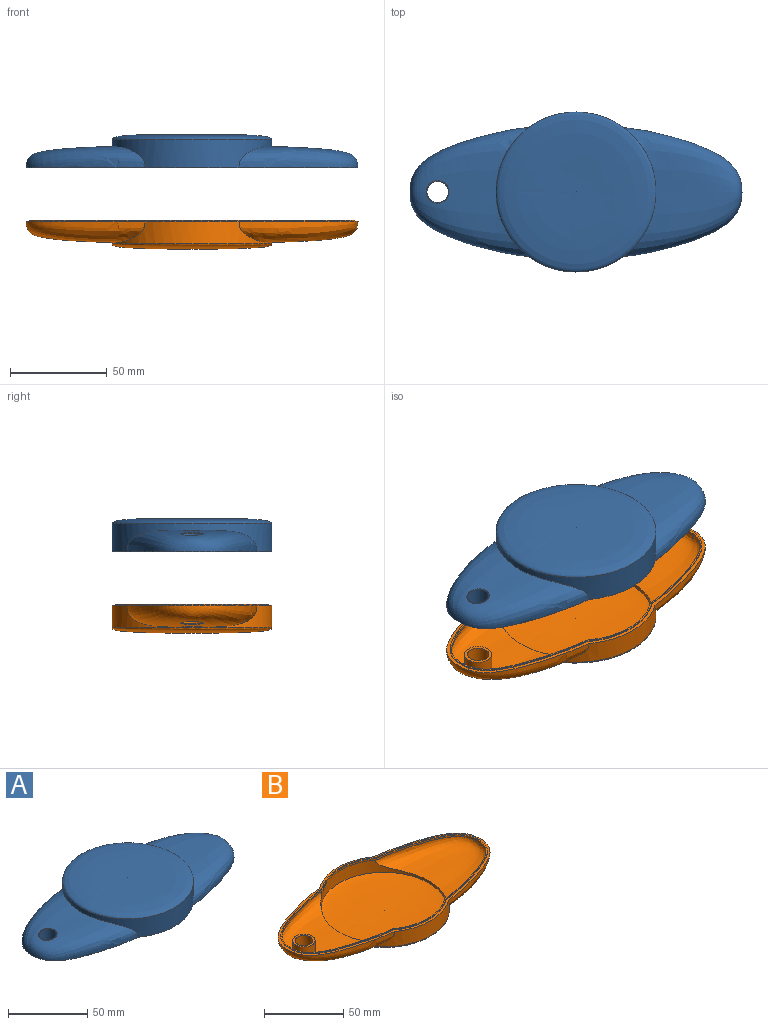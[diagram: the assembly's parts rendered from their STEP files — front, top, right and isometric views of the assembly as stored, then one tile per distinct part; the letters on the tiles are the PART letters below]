
ASSEMBLY  parts=2 mates=1
PART A: 13 faces, bbox 174.5x85.6x22.7 mm
  f0: plane 14.11x14.11mm, normal (0,0,-1), area 59.4mm2, adj f4,f11
  f1: cylinder r=41.28mm len=82.55mm, axis (0,0,1), area 2238.9mm2, adj f2,f3,f5,f7
  f2: revolved ~82.55x82.55mm, area 5526.4mm2, adj f1
  f3: bspline ~66.68x61.39mm, area 3034.7mm2, adj f1,f6,f7
  f4: cylinder r=5.56mm len=11.11mm, axis (0,0,1), area 307mm2, adj f0,f6
  f5: bspline ~66.68x61.39mm, area 3141.8mm2, adj f1,f7
  f6: bspline ~11.65x11.65mm, area 14.6mm2, adj f3,f4
  f7: plane 171.45x82.55mm, normal (0,0,-1), area 601mm2, adj f1,f3,f5,f8,f10,f12
  f8: cylinder r=39.78mm len=79.55mm, axis (0,0,1), area 2268.9mm2, adj f7,f9,f10,f12
  f9: revolved ~0x0mm, area 0mm2, adj f8
  f10: offset ~69.77x65.92mm, area 2725.3mm2, adj f7,f8,f11
  f11: cylinder r=7.06mm len=14.11mm, axis (0,0,1), area 327.9mm2, adj f0,f10
  f12: offset ~69.77x65.83mm, area 2884.3mm2, adj f7,f8
PART B: 27 faces, bbox 180.7x91.8x26.4 mm
  f0: offset ~69.77x65.92mm, area 2784.3mm2, adj f2,f12,f13
  f1: offset ~69.67x64.39mm, area 2909.3mm2, adj f2,f13
  f2: cylinder r=39.78mm len=79.55mm, axis (0,0,1), area 1489.5mm2, adj f0,f1,f11,f13
  f3: plane 14.11x14.11mm, normal (0,0,1), area 59.4mm2, adj f9,f12
  f4: revolved ~82.55x82.55mm, area 5543.5mm2, adj f7
  f5: bspline ~66.68x61.39mm, area 3034.7mm2, adj f7,f8,f10
  f6: bspline ~66.68x61.39mm, area 3050.9mm2, adj f7,f10
  f7: cylinder r=41.28mm len=82.55mm, axis (0,0,1), area 1480.6mm2, adj f4,f5,f6,f10
  f8: bspline ~11.65x11.65mm, area 14.6mm2, adj f5,f9
  f9: cylinder r=5.56mm len=11.11mm, axis (0,0,1), area 307mm2, adj f3,f8
  f10: plane 180.71x91.81mm, normal (0,0,1), area 701.5mm2, adj f5,f6,f7,f21,f22,f23,f24,f25
  f11: revolved ~0x0mm, area 0mm2, adj f2
  f12: cylinder r=7.06mm len=14.11mm, axis (0,0,1), area 327.9mm2, adj f0,f3
  f13: plane 169.29x80.43mm, normal (0,0,-1), area 408.5mm2, adj f0,f1,f2,f15,f16,f17,f18,f19
  f14: plane 168.26x79.36mm, normal (0,0,1), area 307.8mm2, adj f15,f16,f17,f18,f19,f20,f21,f22
  f15: extruded ~59.79x30.89mm, area 90.6mm2, adj f13,f14,f16,f20
  f16: cylinder r=38.78mm len=46.64mm, axis (0,0,-1), area 62.6mm2, adj f13,f14,f15,f17
  f17: extruded ~59.79x30.89mm, area 90.6mm2, adj f13,f14,f16,f18
  f18: extruded ~59.79x30.89mm, area 90.6mm2, adj f13,f14,f17,f19
  f19: cylinder r=38.78mm len=47.15mm, axis (0,0,-1), area 63.4mm2, adj f13,f14,f18,f20
  f20: extruded ~59.28x30.86mm, area 90mm2, adj f13,f14,f15,f19
  f21: cylinder r=39.52mm len=47.42mm, axis (0,0,-1), area 25.4mm2, adj f10,f14,f22,f26
  f22: extruded ~60.26x31.62mm, area 36.7mm2, adj f10,f14,f21,f23
  f23: extruded ~60.26x31.62mm, area 36.7mm2, adj f10,f14,f22,f24
  f24: cylinder r=39.52mm len=47.42mm, axis (0,0,-1), area 25.4mm2, adj f10,f14,f23,f25
  f25: extruded ~60.26x31.62mm, area 36.7mm2, adj f10,f14,f24,f26
  f26: extruded ~60.26x31.62mm, area 36.7mm2, adj f10,f14,f21,f25
PLACE A t=(4.34,70.48,-280.66)mm
PLACE B t=(4.34,70.48,-308.5)mm
MATE slider B.f10 <-> A.f7  axis (0,0,1) through (-81.38,70.48,-309.77)mm
